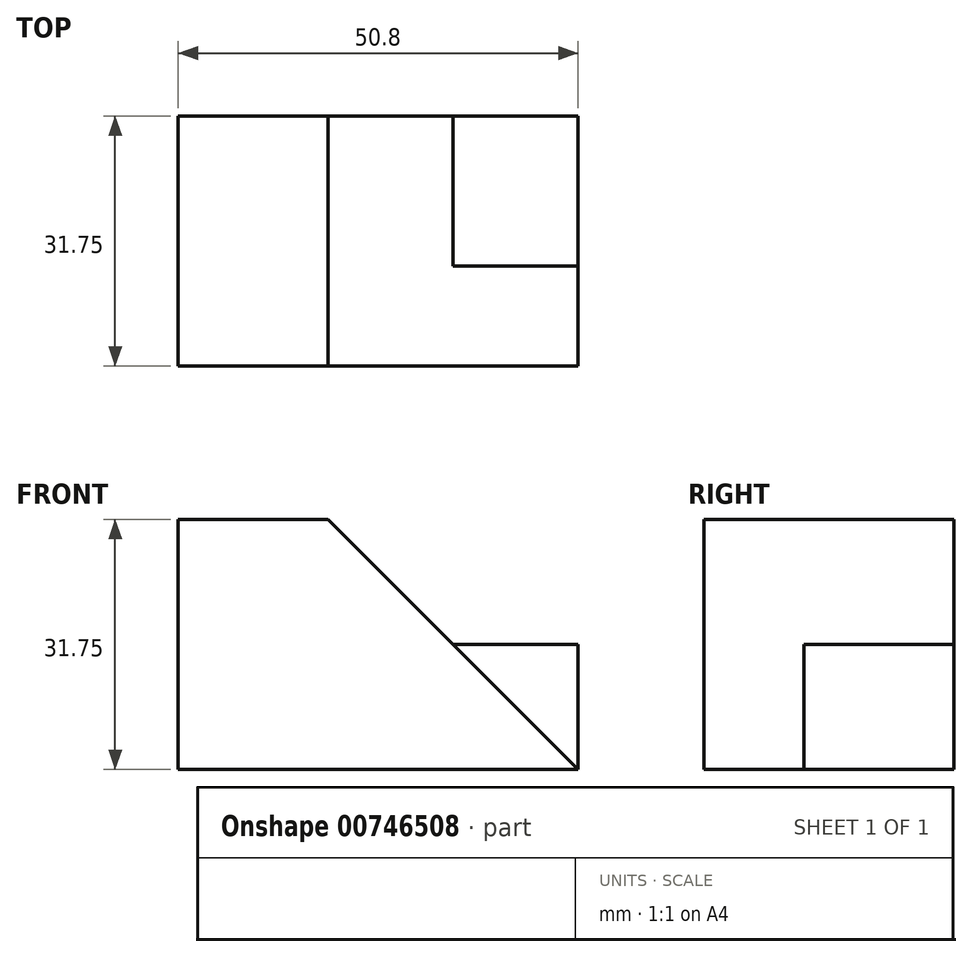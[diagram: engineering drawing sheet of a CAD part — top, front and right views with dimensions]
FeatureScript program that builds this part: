
annotation { "Feature Type Name" : "Feature", "Feature Type Description" : "" }
export const myFeature = defineFeature(function(context is Context, id is Id, definition is map)
    precondition{}
    {
        {
            var Q0;
            Q0=qCreatedBy(makeId("Front.planeOp"),FACE);
            var sketch = newSketch(context, id + "F0", { "sketchPlane" : qUnion([Q0])});
            skLineSegment(sketch, "E0", {"start": v(0, 0) * mm, "end": v(0, 31.75) * mm});
            skLineSegment(sketch, "E1", {"start": v(0, 31.75) * mm, "end": v(50.8, 31.75) * mm});
            skLineSegment(sketch, "E2", {"start": v(50.8, 31.75) * mm, "end": v(50.8, 0) * mm});
            skLineSegment(sketch, "E3", {"start": v(50.8, 0) * mm, "end": v(0, 0) * mm});
            skSolve(sketch);
        }
        {
            var Q0;
            Q0=makeQuery(id+"F0.imprint","IMPRINT",FACE,{"disambiguationData":[TD([[makeQuery(id+"F0.imprint","IMPRINT",EDGE,{"derivedFrom":sQuery(id+"F0.wireOp",EDGE,"E0")}),-1.0]])]});
            extrude(context, id + "F1", {"entities" : qUnion([Q0]), "depth" : 31.75 * mm, "offsetDistance" : 25.4 * mm});
        }
        {
            var Q0;
            Q0=makeQuery(id+"F1.opExtrude","CAP_FACE",FACE,{"disambiguationData":[OSD([sQuery(id+"F0.wireOp",EDGE,"E0"),sQuery(id+"F0.wireOp",EDGE,"E1"),sQuery(id+"F0.wireOp",EDGE,"E2"),sQuery(id+"F0.wireOp",EDGE,"E3")])],"isStart":false});
            var sketch = newSketch(context, id + "F2", { "sketchPlane" : qUnion([Q0])});
            skLineSegment(sketch, "E4", {"start": v(50.8, 0) * mm, "end": v(19.05, 31.75) * mm});
            skLineSegment(sketch, "E5", {"start": v(19.05, 31.75) * mm, "end": v(50.8, 31.75) * mm});
            skLineSegment(sketch, "E6", {"start": v(50.8, 31.75) * mm, "end": v(50.8, 0) * mm});
            skSolve(sketch);
        }
        {
            var Q0;
            Q0 = qSketchRegion(id + "F2", true);
            extrude(context, id + "F3", {"entities" : qUnion([Q0]), "operationType" : NewBodyOperationType.REMOVE, "oppositeDirection" : true, "depth" : 12.7 * mm, "offsetDistance" : 25.4 * mm});
        }
        {
            var Q0;
            Q0=makeQuery(id+"F3.boolean.opBoolean","COPY",FACE,{"derivedFrom":makeQuery(id+"F3.opExtrude","CAP_FACE",FACE,{"disambiguationData":[OSD([sQuery(id+"F2.wireOp",EDGE,"E4"),sQuery(id+"F2.wireOp",EDGE,"E5"),sQuery(id+"F2.wireOp",EDGE,"E6")])],"isStart":false})});
            var sketch = newSketch(context, id + "F4", { "sketchPlane" : qUnion([Q0])});
            skLineSegment(sketch, "E7", {"start": v(19.05, 31.75) * mm, "end": v(34.93, 15.87) * mm});
            skLineSegment(sketch, "E8", {"start": v(34.93, 15.87) * mm, "end": v(34.93, 31.75) * mm});
            skLineSegment(sketch, "E9", {"start": v(34.93, 31.75) * mm, "end": v(19.05, 31.75) * mm});
            skSolve(sketch);
        }
        {
            var Q0;
            Q0=makeQuery(id+"F4.imprint","IMPRINT",FACE,{"disambiguationData":[TD([[makeQuery(id+"F4.imprint","IMPRINT",EDGE,{"derivedFrom":sQuery(id+"F4.wireOp",EDGE,"E7")}),-1.0]])]});
            extrude(context, id + "F5", {"entities" : qUnion([Q0]), "operationType" : NewBodyOperationType.REMOVE, "oppositeDirection" : true, "depth" : 25.4 * mm, "offsetDistance" : 25.4 * mm});
        }
        {
            var Q0;
            Q0=makeQuery(id+"F3.boolean.opBoolean","COPY",FACE,{"derivedFrom":makeQuery(id+"F3.opExtrude","CAP_FACE",FACE,{"disambiguationData":[OSD([sQuery(id+"F2.wireOp",EDGE,"E4"),sQuery(id+"F2.wireOp",EDGE,"E5"),sQuery(id+"F2.wireOp",EDGE,"E6")])],"isStart":false})});
            var sketch = newSketch(context, id + "F6", { "sketchPlane" : qUnion([Q0])});
            skLineSegment(sketch, "E10", {"start": v(34.93, 15.87) * mm, "end": v(50.8, 15.88) * mm});
            skLineSegment(sketch, "E11", {"start": v(50.8, 15.88) * mm, "end": v(50.8, 0) * mm});
            skLineSegment(sketch, "E12", {"start": v(50.8, 0) * mm, "end": v(34.93, 15.87) * mm});
            skSolve(sketch);
        }
        {
            var Q0;
            {var subQ0=sQuery(id+"F6.wireOp",EDGE,"E10");Q0=makeQuery(id+"F6.imprint","IMPRINT",FACE,{"disambiguationData":[TD([[makeQuery(id+"F6.imprint","IMPRINT",EDGE,{"derivedFrom":subQ0}),1.0]])]});}
            extrude(context, id + "F7", {"entities" : qUnion([Q0]), "operationType" : NewBodyOperationType.REMOVE, "oppositeDirection" : true, "depth" : 25.4 * mm, "offsetDistance" : 25.4 * mm});
        }
    });
